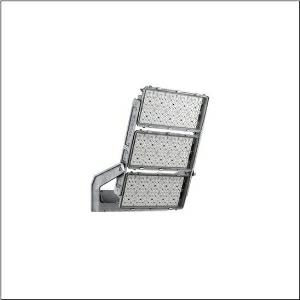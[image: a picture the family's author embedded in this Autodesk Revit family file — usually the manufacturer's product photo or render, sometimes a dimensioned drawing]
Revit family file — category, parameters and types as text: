
# Revit family: floodlight_fl_11_maxi_pro___pl43_5xa779127a01aa_57cb
name_source: partatom
category: Lighting Fixtures
units: mm (PartAtom-declared; Revit-internal decimal feet)

## family parameters
Cut with Voids When Loaded = No
Host = Face
Light Source = No
Part Type = Normal
Room Calculation Point = No
Round Connector Dimension = Use Diameter
Shared = No

## types (1)
- --- (1 x LED, 177380 lm, 1425.5 W, 5000K)
    Apparent Load = 1425 VA
    CIE Flux Codes = 25 74 99 100 100
    Color Rendering = 70
    Color Temperature = 5000K
    Default Elevation = 1800 mm
    Description = Floodlight FL 11  maxi  pro floodlight; light control with lens of PMMA; cover panel of toughened safety glass, transparent; light distribution: PL43, asymmetric direct distribution, LEDcolour temperature: 5000K, rated luminous flux: 177.380lm, colour rendering: CRI > 70, light colour: 750; luminous efficacy: 124lm/W; brightness control: DALI 2 (1 DALI address); with terminal, 5-pole, max. 2.5mm², mains connection: 220..240V/380..400V AC, 50/60Hz, surge voltage resistance: line to ground: 10kV, dustproof LED module, LED unit replaceable without ESD environment, ECG replaceable separately, LED unit replaceable, LED unit replaceable on mast without ESD environment, dimming range 10..100%; 1426W floodlight with 3x LED unit of diecast aluminium, coated grey; length: 1.003mm / width: 651mm / height: 338mm; mounting bracket, of diecast aluminium, uncoated, natural, equipment: Power, protection rating (complete): IP66; insulation class (complete): insulation class I (protective earthing); certification: CE, ENEC, VDE; ball protection: ball impact resistant, impact resistance: IK07; rated ambient temperature 10°C, only for outdoor installations, permissible operating ambient temperature: -40..+30°C, permissible storage temperature: -40..+85°Cpackaging unit: 1 piece

Light Distribution: PL43
    Height = 320 mm
    Lamp = 1 x LED
    Lamp Light Flux = 177380 lm
    Lamp Power = 1425.5 W
    Lamp count = 1
    Length = 1002 mm
    Luminous efficacy = 124 lm/W
    Manufacturer = Siteco
    ModVariant = No
    Model = 5XA779127A01AA
    Mounting Place = Ceiling
    Mounting Type = Surface mounted
    Number of Poles = 1
    OnlyDefault = Yes
    Power Factor = 1
    Product Name = Floodlight FL 11 maxi pro | PL43
    Product group = floodlight | ceiling mounted
    ProductGroupID = 301
    Protection Class = Protection class I
    Protection Degree = IP 66
    RLX_Detail_Level = 1
    RLX_Emergency_Light_Flux = 0 lm
    RLX_Emergency_Type = 0
    RLX_Emergency_Type_DB = No
    RlxData = <blob elided: 51757 chars, md5=dde054e4>
    Socket = socket
    Standby Power = 0 W
    System Light Flux = 177380 lm
    System Power = 1425 W
    Type Comments = factory setting: luminous flux: 100 % | dim-lin: 254 | 980 mA
    Type Image = l_1349137.jpg
    URL = http://relux.com
    VarID = @adj_096722
    Voltage = 0 V
    Weight = 0.00 kg
    Width = 655 mm

## geometry (parser evidence)
native form markers: Blend x4, Sweep x14
no freeform markers — native parametric forms only
